# Revit family: PGR_Noken_WtrSplyFitngsForBdts_Tono
name_source: partatom
category: Plumbing Fixtures
revit_build: Autodesk Revit 2017 (Build: 20190508_0315(x64)
units: mm (PartAtom-declared; Revit-internal decimal feet)

## family parameters
Always vertical = Yes
Cut with Voids When Loaded = No
OmniClass Number = 23.45.55.17
OmniClass Title = Mixing Faucets
Part Type = Normal
Room Calculation Point = No
Round Connector Dimension = Use Diameter
Shared = No
Work Plane-Based = Yes

## types (2) — shared parameters
AccessibilityPerformance = See ProductInformation for technical PDF
ApplicationType = Bidet
AssetType = Fixed
BodyMaterial = Brass
Category = Pr_40_20_87_11: Bidet taps
CloseOffRating = 0.0 Pa
CodePerformance = EN 817, EN 248
Collection = Tono
Color = Chrome
Description = Single lever bidet mixer 3/8”. Ø35 mm ceramic cartridge Length of hoses 440 mm. Without pop-up waste. Flow rate 5.68 l/min. at 3 bar. Material brass, finish chrome plated. 5 years warranty for superficial finishes and 2 years for the rest of components. EN 817, EN 248
DurationUnit = year
FaucetFunction = Mixed
FaucetOperation = LeverHandle
FaucetTopDescription = Lever
FaucetType = Pillar
Features = See ProductInformation for technical PDF
Finish = Chrome
IfcExportAs = IfcValveType
IfcExportType = Faucet
ManufacturerURL = www.noken.com
Material = Brass
MaterialMetal = PGR_Noken_Brass_Chrome
NBSDescription = Water supply fittings for bidets
NBSReference = 45-35-701/323
NominalHeight = 126 mm
NominalLength = 139 mm  [stored 0.456037 ft]
NominalWidth = 48 mm
ProductInformation = http://calidad.info-grupo.com:8081
Reference = -
Size = 42x135x126mm
Status = Unset
SustainabilityPerformance = See ProductInformation for technical PDF
TechnicalDrawing = See ProductInformation for technical PDF
TestPressure = 0.0 Pa
URL = www.noken.com
Uniclass2015Code = Pr_40_20_87_11
Uniclass2015Title = Bidet taps
Uniclass2015Version = V1_9
ValveMechanism = Unset
ValveOperation = Lever
ValvePattern = Unset
Version = 1
WarrantyDescription = See ProductInformation for technical PDF
WarrantyDurationUnit = year
zero-valued in all types: Default Elevation, FlowCoefficient, InletConnectionSize, NettWeight, NumberOfConnections, OutletConnectionSize

## per-type parameters (varying)
| type | BIMObjectName | Model | ModelNumber | ModelReference | Name | Type Image | Vs1 | Vs2 |
| SmoothHandle-100184729 | PGR_Noken_WaterSupplyFittingsForBidets_Tono_Chrome-42x135x126mm-100184729 | 100184729 | 100184729 | MONOMANDO TONO BIDET CROMO | WaterSupplyFittingsForBidets_Tono_Chrome-42x135x126mm-100184729 | 100184729.jpg | Yes | No |
| RibHandle-100184756 | PGR_Noken_WaterSupplyFittingsForBidets_Tono_Chrome-42x135x126mm-100184756 | 100184756 | 100184756 | MONOMANDO TONO BIDET MANETA ESTRIADA CRO | WaterSupplyFittingsForBidets_Tono_Chrome-42x135x126mm-100184756 | 100184756.jpg | No | Yes |

note: [stored X ft] marks values corroborated as IEEE doubles in the binary element streams (Revit-internal decimal feet)

## geometry (parser evidence)
native form markers: Blend x2, Sweep x2
no freeform markers — native parametric forms only
